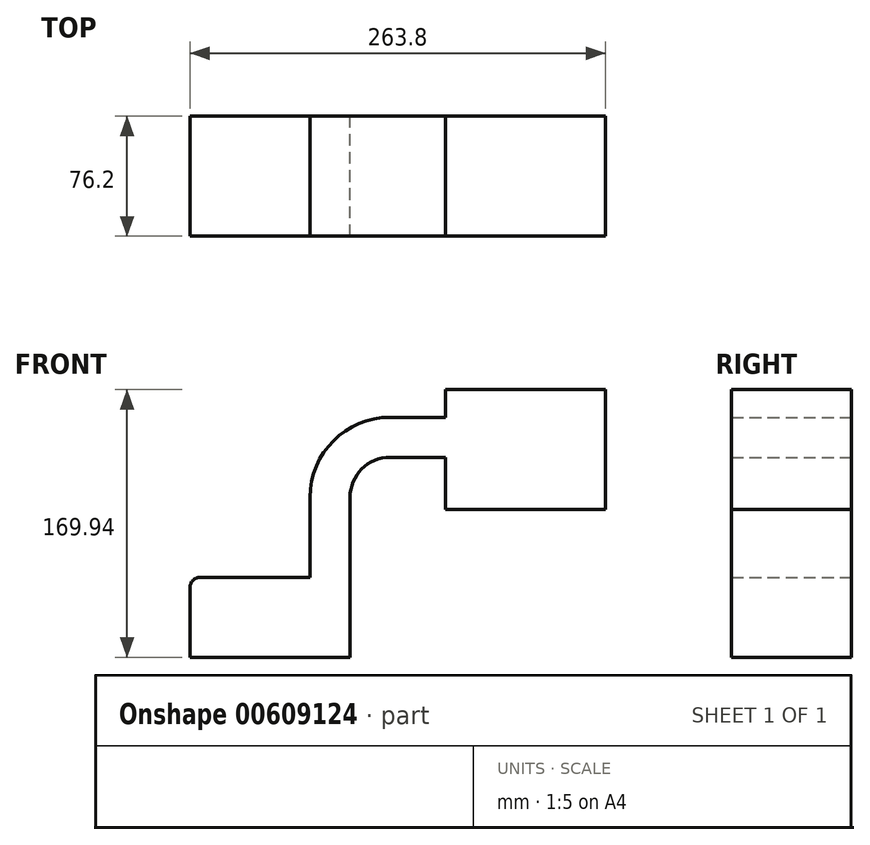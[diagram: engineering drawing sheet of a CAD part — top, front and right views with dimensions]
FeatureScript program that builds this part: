
annotation { "Feature Type Name" : "Feature", "Feature Type Description" : "" }
export const myFeature = defineFeature(function(context is Context, id is Id, definition is map)
    precondition{}
    {
        {
            var Q0;
            Q0=qCreatedBy(makeId("Front.planeOp"),FACE);
            var sketch = newSketch(context, id + "F0", { "sketchPlane" : qUnion([Q0])});
            skLineSegment(sketch, "E0.bottom", {"start": v(50.8, -25.4) * mm, "end": v(-50.8, -25.4) * mm});
            skLineSegment(sketch, "E0.top", {"start": v(50.8, 25.4) * mm, "end": v(-44.45, 25.4) * mm});
            skLineSegment(sketch, "E0.left", {"start": v(50.8, -25.4) * mm, "end": v(50.8, 25.4) * mm});
            skLineSegment(sketch, "E0.right", {"start": v(-50.8, -25.4) * mm, "end": v(-50.8, 19.05) * mm});
            skPoint(sketch, "E0.middle", {"position": v(0, 0) * mm});
            skLineSegment(sketch, "E1.bottom", {"start": v(213, 68.34) * mm, "end": v(111.4, 68.34) * mm});
            skLineSegment(sketch, "E1.top", {"start": v(213, 144.54) * mm, "end": v(111.4, 144.54) * mm});
            skLineSegment(sketch, "E1.left", {"start": v(213, 68.34) * mm, "end": v(213, 144.54) * mm});
            skLineSegment(sketch, "E1.right", {"start": v(111.4, 68.34) * mm, "end": v(111.4, 144.54) * mm});
            skPoint(sketch, "E1.middle", {"position": v(162.2, 106.44) * mm});
            skLineSegment(sketch, "E2", {"start": v(50.8, 25.4) * mm, "end": v(50.8, 76.2) * mm});
            skArc(sketch, "E3", {"start": v(76.2, 101.6) * mm, "mid": v(58.24, 94.16) * mm, "end": v(50.8, 76.2) * mm});
            skLineSegment(sketch, "E4", {"start": v(76.2, 101.6) * mm, "end": v(127.16, 101.6) * mm});
            skLineSegment(sketch, "E5.0", {"start": v(76.2, 95.25) * mm, "end": v(127.16, 95.25) * mm});
            skArc(sketch, "E5.1", {"start": v(76.2, 95.25) * mm, "mid": v(62.73, 89.67) * mm, "end": v(57.15, 76.2) * mm});
            skLineSegment(sketch, "E5.2", {"start": v(57.15, 25.4) * mm, "end": v(57.15, 76.2) * mm});
            skLineSegment(sketch, "E6.0", {"start": v(76.2, 127) * mm, "end": v(127.16, 127) * mm});
            skArc(sketch, "E6.1", {"start": v(76.2, 127) * mm, "mid": v(40.28, 112.12) * mm, "end": v(25.4, 76.2) * mm});
            skLineSegment(sketch, "E6.2", {"start": v(25.4, 25.4) * mm, "end": v(25.4, 76.2) * mm});
            skPoint(sketch, "E7.visualSharp", {"position": v(-50.8, 25.4) * mm});
            skArc(sketch, "E7.filletArc", {"start": v(-44.45, 25.4) * mm, "mid": v(-48.94, 23.54) * mm, "end": v(-50.8, 19.05) * mm});
            skFitSpline(sketch, "E8", {"points": [v(-44.45, 25.4) * mm, v(-13.34, 109.61) * mm, v(111.4, 144.54) * mm], "startDerivative": vector(32.11, 212.93) * mm, "endDerivative": vector(272.26, 30.9) * mm});
            skSolve(sketch);
        }
        {
            var Q0;
            Q0=makeQuery(id+"F0.imprint","IMPRINT",FACE,{"disambiguationData":[TD([[makeQuery(id+"F0.imprint","IMPRINT",EDGE,{"derivedFrom":sQuery(id+"F0.wireOp",EDGE,"E0.bottom")}),-1.0]])]});
            var Q1;
            {var subQ1=sQuery(id+"F0.wireOp",EDGE,"E2");Q1=makeQuery(id+"F0.imprint","IMPRINT",FACE,{"disambiguationData":[TD([[makeQuery(id+"F0.imprint","IMPRINT",EDGE,{"derivedFrom":subQ1}),1.0]])]});}
            var Q2;
            {var subQ1=sQuery(id+"F0.wireOp",EDGE,"E1.bottom");Q2=makeQuery(id+"F0.imprint","IMPRINT",FACE,{"disambiguationData":[TD([[makeQuery(id+"F0.imprint","IMPRINT",EDGE,{"derivedFrom":subQ1}),-1.0]])]});}
            extrude(context, id + "F1", {"entities" : qUnion([Q0, Q1, Q2]), "endBound" : BoundingType.SYMMETRIC, "depth" : 76.2 * mm, "offsetDistance" : 25.4 * mm});
        }
    });
